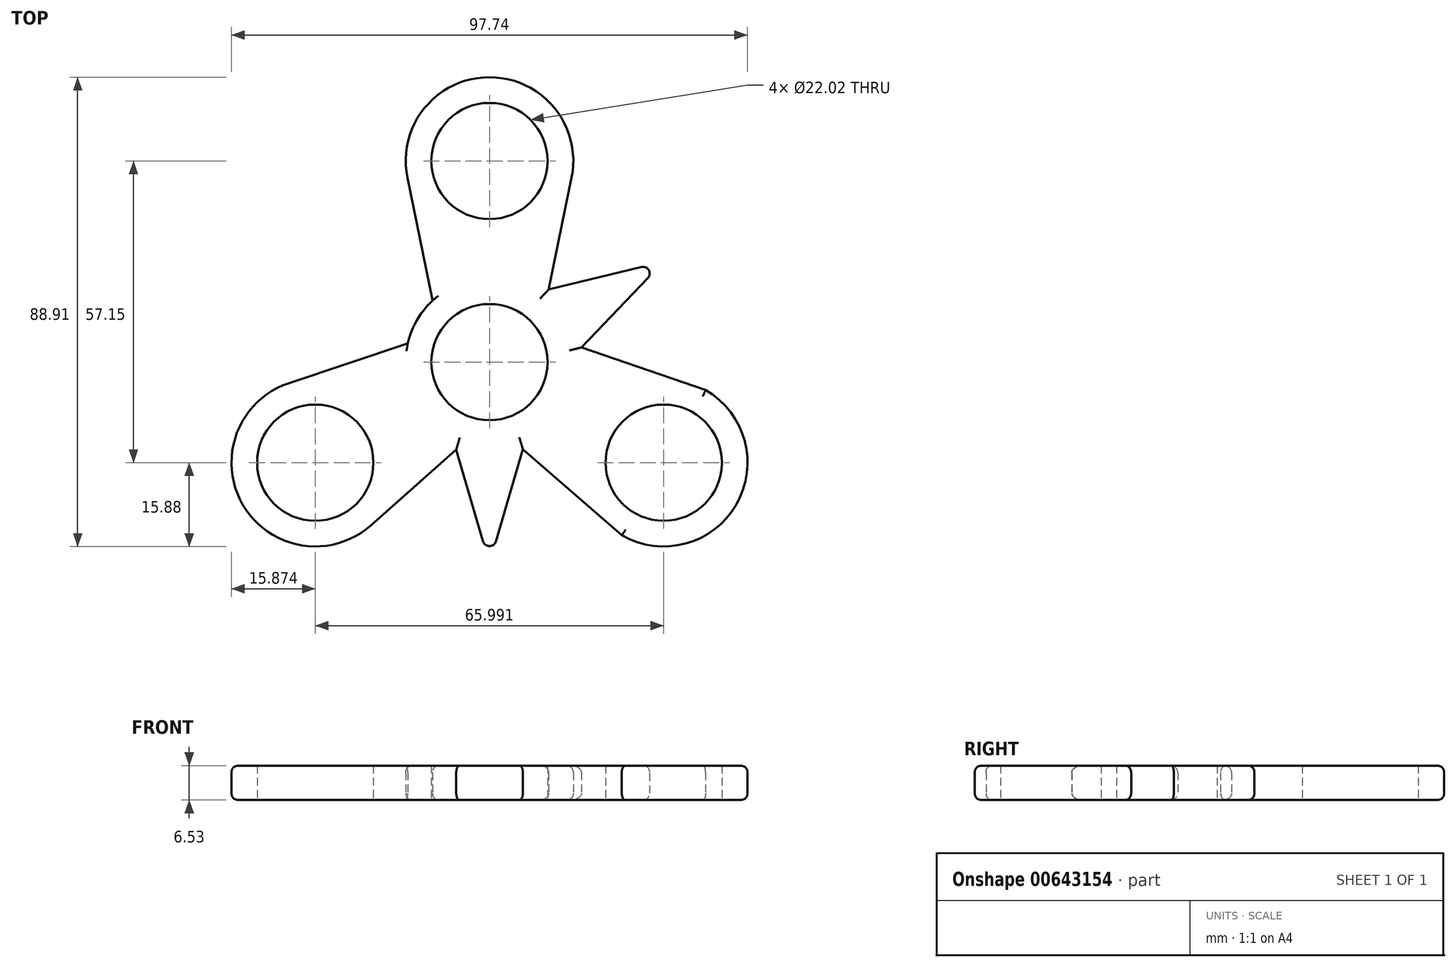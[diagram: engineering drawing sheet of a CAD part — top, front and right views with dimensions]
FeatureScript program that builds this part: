
annotation { "Feature Type Name" : "Feature", "Feature Type Description" : "" }
export const myFeature = defineFeature(function(context is Context, id is Id, definition is map)
    precondition{}
    {
        {
            var Q0;
            Q0=qCreatedBy(makeId("Top.planeOp"),FACE);
            var sketch = newSketch(context, id + "F0", { "sketchPlane" : qUnion([Q0])});
            skCircle(sketch, "E0", {"center": v(0, 0) * mm, "radius": 11.01 * mm});
            skLineSegment(sketch, "E1", {"start": v(0, 0) * mm, "end": v(0, 38.1) * mm});
            skLineSegment(sketch, "E2", {"start": v(0, 0) * mm, "end": v(33, -19.05) * mm});
            skLineSegment(sketch, "E3", {"start": v(0, 0) * mm, "end": v(-33, -19.05) * mm});
            skLineSegment(sketch, "E4", {"start": v(0, 0) * mm, "end": v(-33, 19.05) * mm});
            skLineSegment(sketch, "E5", {"start": v(-33, 19.05) * mm, "end": v(0, 0) * mm});
            skLineSegment(sketch, "E6", {"start": v(0, 0) * mm, "end": v(0, -38.1) * mm});
            skLineSegment(sketch, "E7", {"start": v(0, 0) * mm, "end": v(33, 19.05) * mm});
            skCircle(sketch, "E8", {"center": v(0, 38.1) * mm, "radius": 11.01 * mm});
            skCircle(sketch, "E9", {"center": v(33, -19.05) * mm, "radius": 11.01 * mm});
            skCircle(sketch, "E10", {"center": v(-33, -19.05) * mm, "radius": 11.01 * mm});
            skLineSegment(sketch, "E11", {"start": v(9.54, -5.5) * mm, "end": v(0, -38.1) * mm});
            skLineSegment(sketch, "E12", {"start": v(-9.54, -5.5) * mm, "end": v(0, -38.1) * mm});
            skLineSegment(sketch, "E13", {"start": v(-9.54, -5.5) * mm, "end": v(-33, 19.05) * mm});
            skLineSegment(sketch, "E14", {"start": v(0, 11.01) * mm, "end": v(-33, 19.05) * mm});
            skLineSegment(sketch, "E15", {"start": v(-9.54, 5.5) * mm, "end": v(-33, -19.05) * mm});
            skLineSegment(sketch, "E16", {"start": v(0, -11.01) * mm, "end": v(-33, -19.05) * mm});
            skLineSegment(sketch, "E17", {"start": v(9.54, 5.5) * mm, "end": v(33, -19.05) * mm});
            skLineSegment(sketch, "E18", {"start": v(0, -11.01) * mm, "end": v(33, -19.05) * mm});
            skLineSegment(sketch, "E19", {"start": v(0, 11.01) * mm, "end": v(33, 19.05) * mm});
            skLineSegment(sketch, "E20", {"start": v(9.54, -5.5) * mm, "end": v(33, 19.05) * mm});
            skLineSegment(sketch, "E21", {"start": v(9.54, 5.5) * mm, "end": v(0, 38.1) * mm});
            skLineSegment(sketch, "E22", {"start": v(-9.54, 5.5) * mm, "end": v(0, 38.1) * mm});
            skCircle(sketch, "E23", {"center": v(0, 0) * mm, "radius": 15.88 * mm});
            skCircle(sketch, "E24", {"center": v(0, 38.1) * mm, "radius": 15.88 * mm});
            skCircle(sketch, "E25", {"center": v(33, -19.05) * mm, "radius": 15.88 * mm});
            skCircle(sketch, "E26", {"center": v(-33, -19.05) * mm, "radius": 15.88 * mm});
            skLineSegment(sketch, "E27", {"start": v(-41.1, -5.02) * mm, "end": v(-24.9, -33.08) * mm});
            skLineSegment(sketch, "E28", {"start": v(-9.54, 5.5) * mm, "end": v(-41.1, -5.02) * mm});
            skLineSegment(sketch, "E29", {"start": v(0, -11.01) * mm, "end": v(-24.9, -33.08) * mm});
            skLineSegment(sketch, "E30", {"start": v(0, -11.01) * mm, "end": v(25.06, -32.8) * mm});
            skLineSegment(sketch, "E31", {"start": v(9.54, 5.5) * mm, "end": v(40.93, -5.3) * mm});
            skLineSegment(sketch, "E32", {"start": v(-16.2, 38.1) * mm, "end": v(16.2, 38.1) * mm});
            skLineSegment(sketch, "E33", {"start": v(9.54, 5.5) * mm, "end": v(16.2, 38.1) * mm});
            skLineSegment(sketch, "E34", {"start": v(-9.54, 5.5) * mm, "end": v(-16.2, 38.1) * mm});
            skLineSegment(sketch, "E35", {"start": v(25.06, -32.8) * mm, "end": v(40.93, -5.3) * mm});
            skSolve(sketch);
        }
        {
            var Q0;
            {var subQ0=sQuery(id+"F0.wireOp",EDGE,"E14");var subQ3=sQuery(id+"F0.wireOp",EDGE,"E22");var subQ5=makeQuery(id+"F0.imprint","INTERSECT",VERTEX,{"derivedFrom":[subQ0,subQ3]});Q0=makeQuery(id+"F0.imprint","IMPRINT",FACE,{"disambiguationData":[TD([[makeQuery(id+"F0.imprint","IMPRINT",EDGE,{"disambiguationData":[TD([[subQ5,1.0]])],"derivedFrom":subQ0}),1.0]])]});}
            var Q1;
            {var subQ1=sQuery(id+"F0.wireOp",EDGE,"E5");var subQ3=sQuery(id+"F0.wireOp",EDGE,"E23");var subQ4=makeQuery(id+"F0.imprint","INTERSECT",VERTEX,{"derivedFrom":[subQ1,subQ3]});Q1=makeQuery(id+"F0.imprint","IMPRINT",FACE,{"disambiguationData":[TD([[makeQuery(id+"F0.imprint","IMPRINT",EDGE,{"disambiguationData":[TD([[subQ4,1.0]])],"derivedFrom":subQ3}),-1.0]])]});}
            var Q2;
            {var subQ1=sQuery(id+"F0.wireOp",EDGE,"E5");var subQ3=sQuery(id+"F0.wireOp",EDGE,"E23");var subQ4=makeQuery(id+"F0.imprint","INTERSECT",VERTEX,{"derivedFrom":[subQ1,subQ3]});Q2=makeQuery(id+"F0.imprint","IMPRINT",FACE,{"disambiguationData":[TD([[makeQuery(id+"F0.imprint","IMPRINT",EDGE,{"disambiguationData":[TD([[subQ4,-1.0]])],"derivedFrom":subQ3}),-1.0]])]});}
            var Q3;
            {var subQ1=sQuery(id+"F0.wireOp",EDGE,"E5");var subQ3=sQuery(id+"F0.wireOp",EDGE,"E23");var subQ4=makeQuery(id+"F0.imprint","INTERSECT",VERTEX,{"derivedFrom":[subQ1,subQ3]});Q3=makeQuery(id+"F0.imprint","IMPRINT",FACE,{"disambiguationData":[TD([[makeQuery(id+"F0.imprint","IMPRINT",EDGE,{"disambiguationData":[TD([[subQ4,-1.0]])],"derivedFrom":subQ3}),1.0]])]});}
            var Q4;
            {var subQ0=sQuery(id+"F0.wireOp",EDGE,"E15");var subQ1=sQuery(id+"F0.wireOp",EDGE,"E13");var subQ2=makeQuery(id+"F0.imprint","INTERSECT",VERTEX,{"derivedFrom":[subQ1,subQ0]});Q4=makeQuery(id+"F0.imprint","IMPRINT",FACE,{"disambiguationData":[TD([[makeQuery(id+"F0.imprint","IMPRINT",EDGE,{"disambiguationData":[TD([[subQ2,-1.0]])],"derivedFrom":subQ1}),-1.0]])]});}
            var Q5;
            {var subQ0=sQuery(id+"F0.wireOp",EDGE,"E13");var subQ3=sQuery(id+"F0.wireOp",EDGE,"E15");var subQ5=makeQuery(id+"F0.imprint","INTERSECT",VERTEX,{"derivedFrom":[subQ0,subQ3]});Q5=makeQuery(id+"F0.imprint","IMPRINT",FACE,{"disambiguationData":[TD([[makeQuery(id+"F0.imprint","IMPRINT",EDGE,{"disambiguationData":[TD([[subQ5,1.0]])],"derivedFrom":subQ0}),-1.0]])]});}
            var Q6;
            {var subQ1=sQuery(id+"F0.wireOp",EDGE,"E5");var subQ3=sQuery(id+"F0.wireOp",EDGE,"E23");var subQ4=makeQuery(id+"F0.imprint","INTERSECT",VERTEX,{"derivedFrom":[subQ1,subQ3]});Q6=makeQuery(id+"F0.imprint","IMPRINT",FACE,{"disambiguationData":[TD([[makeQuery(id+"F0.imprint","IMPRINT",EDGE,{"disambiguationData":[TD([[subQ4,1.0]])],"derivedFrom":subQ3}),1.0]])]});}
            var Q7;
            {var subQ0=sQuery(id+"F0.wireOp",EDGE,"E34");var subQ1=sQuery(id+"F0.wireOp",EDGE,"E14");var subQ2=makeQuery(id+"F0.imprint","INTERSECT",VERTEX,{"derivedFrom":[subQ1,subQ0]});Q7=makeQuery(id+"F0.imprint","IMPRINT",FACE,{"disambiguationData":[TD([[makeQuery(id+"F0.imprint","IMPRINT",EDGE,{"disambiguationData":[TD([[subQ2,1.0]])],"derivedFrom":subQ1}),1.0]])]});}
            var Q8;
            {var subQ0=sQuery(id+"F0.wireOp",EDGE,"E22");var subQ1=sQuery(id+"F0.wireOp",EDGE,"E14");var subQ2=makeQuery(id+"F0.imprint","INTERSECT",VERTEX,{"derivedFrom":[subQ1,subQ0]});Q8=makeQuery(id+"F0.imprint","IMPRINT",FACE,{"disambiguationData":[TD([[makeQuery(id+"F0.imprint","IMPRINT",EDGE,{"disambiguationData":[TD([[subQ2,-1.0]])],"derivedFrom":subQ1}),1.0]])]});}
            var Q9;
            {var subQ0=sQuery(id+"F0.wireOp",EDGE,"E34");var subQ5=sQuery(id+"F0.wireOp",EDGE,"E14");var subQ6=makeQuery(id+"F0.imprint","INTERSECT",VERTEX,{"derivedFrom":[subQ5,subQ0]});Q9=makeQuery(id+"F0.imprint","IMPRINT",FACE,{"disambiguationData":[TD([[makeQuery(id+"F0.imprint","IMPRINT",EDGE,{"disambiguationData":[TD([[subQ6,1.0]])],"derivedFrom":subQ5}),-1.0]])]});}
            var Q10;
            {var subQ0=sQuery(id+"F0.wireOp",EDGE,"E23");var subQ1=sQuery(id+"F0.wireOp",EDGE,"E1");var subQ2=makeQuery(id+"F0.imprint","INTERSECT",VERTEX,{"derivedFrom":[subQ1,subQ0]});Q10=makeQuery(id+"F0.imprint","IMPRINT",FACE,{"disambiguationData":[TD([[makeQuery(id+"F0.imprint","IMPRINT",EDGE,{"disambiguationData":[TD([[subQ2,-1.0]])],"derivedFrom":subQ1}),1.0]])]});}
            var Q11;
            {var subQ0=sQuery(id+"F0.wireOp",EDGE,"E19");var subQ5=sQuery(id+"F0.wireOp",EDGE,"E21");var subQ6=makeQuery(id+"F0.imprint","INTERSECT",VERTEX,{"derivedFrom":[subQ0,subQ5]});Q11=makeQuery(id+"F0.imprint","IMPRINT",FACE,{"disambiguationData":[TD([[makeQuery(id+"F0.imprint","IMPRINT",EDGE,{"disambiguationData":[TD([[subQ6,-1.0]])],"derivedFrom":subQ5}),1.0]])]});}
            var Q12;
            {var subQ0=sQuery(id+"F0.wireOp",EDGE,"E14");var subQ5=sQuery(id+"F0.wireOp",EDGE,"E22");var subQ6=makeQuery(id+"F0.imprint","INTERSECT",VERTEX,{"derivedFrom":[subQ0,subQ5]});Q12=makeQuery(id+"F0.imprint","IMPRINT",FACE,{"disambiguationData":[TD([[makeQuery(id+"F0.imprint","IMPRINT",EDGE,{"disambiguationData":[TD([[subQ6,-1.0]])],"derivedFrom":subQ5}),-1.0]])]});}
            var Q13;
            {var subQ0=sQuery(id+"F0.wireOp",EDGE,"E22");var subQ1=sQuery(id+"F0.wireOp",EDGE,"E14");var subQ2=makeQuery(id+"F0.imprint","INTERSECT",VERTEX,{"derivedFrom":[subQ1,subQ0]});Q13=makeQuery(id+"F0.imprint","IMPRINT",FACE,{"disambiguationData":[TD([[makeQuery(id+"F0.imprint","IMPRINT",EDGE,{"disambiguationData":[TD([[subQ2,-1.0]])],"derivedFrom":subQ1}),-1.0]])]});}
            var Q14;
            {var subQ0=sQuery(id+"F0.wireOp",EDGE,"E28");var subQ1=sQuery(id+"F0.wireOp",EDGE,"E13");var subQ2=makeQuery(id+"F0.imprint","INTERSECT",VERTEX,{"derivedFrom":[subQ1,subQ0]});Q14=makeQuery(id+"F0.imprint","IMPRINT",FACE,{"disambiguationData":[TD([[makeQuery(id+"F0.imprint","IMPRINT",EDGE,{"disambiguationData":[TD([[subQ2,1.0]])],"derivedFrom":subQ1}),-1.0]])]});}
            var Q15;
            {var subQ0=sQuery(id+"F0.wireOp",EDGE,"E28");var subQ6=sQuery(id+"F0.wireOp",EDGE,"E13");var subQ9=makeQuery(id+"F0.imprint","INTERSECT",VERTEX,{"derivedFrom":[subQ6,subQ0]});Q15=makeQuery(id+"F0.imprint","IMPRINT",FACE,{"disambiguationData":[TD([[makeQuery(id+"F0.imprint","IMPRINT",EDGE,{"disambiguationData":[TD([[subQ9,1.0]])],"derivedFrom":subQ6}),1.0]])]});}
            var Q16;
            {var subQ0=sQuery(id+"F0.wireOp",EDGE,"E13");var subQ5=sQuery(id+"F0.wireOp",EDGE,"E15");var subQ6=makeQuery(id+"F0.imprint","INTERSECT",VERTEX,{"derivedFrom":[subQ0,subQ5]});Q16=makeQuery(id+"F0.imprint","IMPRINT",FACE,{"disambiguationData":[TD([[makeQuery(id+"F0.imprint","IMPRINT",EDGE,{"disambiguationData":[TD([[subQ6,-1.0]])],"derivedFrom":subQ5}),1.0]])]});}
            var Q17;
            {var subQ0=sQuery(id+"F0.wireOp",EDGE,"E15");var subQ1=sQuery(id+"F0.wireOp",EDGE,"E13");var subQ2=makeQuery(id+"F0.imprint","INTERSECT",VERTEX,{"derivedFrom":[subQ1,subQ0]});Q17=makeQuery(id+"F0.imprint","IMPRINT",FACE,{"disambiguationData":[TD([[makeQuery(id+"F0.imprint","IMPRINT",EDGE,{"disambiguationData":[TD([[subQ2,-1.0]])],"derivedFrom":subQ1}),1.0]])]});}
            var Q18;
            {var subQ0=sQuery(id+"F0.wireOp",EDGE,"E23");var subQ1=sQuery(id+"F0.wireOp",EDGE,"E3");var subQ2=makeQuery(id+"F0.imprint","INTERSECT",VERTEX,{"derivedFrom":[subQ1,subQ0]});Q18=makeQuery(id+"F0.imprint","IMPRINT",FACE,{"disambiguationData":[TD([[makeQuery(id+"F0.imprint","IMPRINT",EDGE,{"disambiguationData":[TD([[subQ2,-1.0]])],"derivedFrom":subQ1}),-1.0]])]});}
            var Q19;
            {var subQ0=sQuery(id+"F0.wireOp",EDGE,"E16");var subQ1=sQuery(id+"F0.wireOp",EDGE,"E12");var subQ2=makeQuery(id+"F0.imprint","INTERSECT",VERTEX,{"derivedFrom":[subQ1,subQ0]});Q19=makeQuery(id+"F0.imprint","IMPRINT",FACE,{"disambiguationData":[TD([[makeQuery(id+"F0.imprint","IMPRINT",EDGE,{"disambiguationData":[TD([[subQ2,-1.0]])],"derivedFrom":subQ1}),1.0]])]});}
            var Q20;
            {var subQ1=sQuery(id+"F0.wireOp",EDGE,"E6");var subQ3=sQuery(id+"F0.wireOp",EDGE,"E23");var subQ4=makeQuery(id+"F0.imprint","INTERSECT",VERTEX,{"derivedFrom":[subQ1,subQ3]});Q20=makeQuery(id+"F0.imprint","IMPRINT",FACE,{"disambiguationData":[TD([[makeQuery(id+"F0.imprint","IMPRINT",EDGE,{"disambiguationData":[TD([[subQ4,1.0]])],"derivedFrom":subQ3}),1.0]])]});}
            var Q21;
            {var subQ1=sQuery(id+"F0.wireOp",EDGE,"E6");var subQ3=sQuery(id+"F0.wireOp",EDGE,"E23");var subQ4=makeQuery(id+"F0.imprint","INTERSECT",VERTEX,{"derivedFrom":[subQ1,subQ3]});Q21=makeQuery(id+"F0.imprint","IMPRINT",FACE,{"disambiguationData":[TD([[makeQuery(id+"F0.imprint","IMPRINT",EDGE,{"disambiguationData":[TD([[subQ4,-1.0]])],"derivedFrom":subQ3}),1.0]])]});}
            var Q22;
            {var subQ0=sQuery(id+"F0.wireOp",EDGE,"E18");var subQ1=sQuery(id+"F0.wireOp",EDGE,"E11");var subQ2=makeQuery(id+"F0.imprint","INTERSECT",VERTEX,{"derivedFrom":[subQ1,subQ0]});Q22=makeQuery(id+"F0.imprint","IMPRINT",FACE,{"disambiguationData":[TD([[makeQuery(id+"F0.imprint","IMPRINT",EDGE,{"disambiguationData":[TD([[subQ2,-1.0]])],"derivedFrom":subQ1}),-1.0]])]});}
            var Q23;
            {var subQ0=sQuery(id+"F0.wireOp",EDGE,"E18");var subQ1=sQuery(id+"F0.wireOp",EDGE,"E11");var subQ2=makeQuery(id+"F0.imprint","INTERSECT",VERTEX,{"derivedFrom":[subQ1,subQ0]});Q23=makeQuery(id+"F0.imprint","IMPRINT",FACE,{"disambiguationData":[TD([[makeQuery(id+"F0.imprint","IMPRINT",EDGE,{"disambiguationData":[TD([[subQ2,-1.0]])],"derivedFrom":subQ1}),1.0]])]});}
            var Q24;
            {var subQ0=sQuery(id+"F0.wireOp",EDGE,"E16");var subQ1=sQuery(id+"F0.wireOp",EDGE,"E12");var subQ2=makeQuery(id+"F0.imprint","INTERSECT",VERTEX,{"derivedFrom":[subQ1,subQ0]});Q24=makeQuery(id+"F0.imprint","IMPRINT",FACE,{"disambiguationData":[TD([[makeQuery(id+"F0.imprint","IMPRINT",EDGE,{"disambiguationData":[TD([[subQ2,-1.0]])],"derivedFrom":subQ1}),-1.0]])]});}
            var Q25;
            {var subQ0=sQuery(id+"F0.wireOp",EDGE,"E12");var subQ3=sQuery(id+"F0.wireOp",EDGE,"E16");var subQ5=makeQuery(id+"F0.imprint","INTERSECT",VERTEX,{"derivedFrom":[subQ0,subQ3]});Q25=makeQuery(id+"F0.imprint","IMPRINT",FACE,{"disambiguationData":[TD([[makeQuery(id+"F0.imprint","IMPRINT",EDGE,{"disambiguationData":[TD([[subQ5,1.0]])],"derivedFrom":subQ0}),1.0]])]});}
            var Q26;
            {var subQ0=sQuery(id+"F0.wireOp",EDGE,"E12");var subQ5=sQuery(id+"F0.wireOp",EDGE,"E16");var subQ6=makeQuery(id+"F0.imprint","INTERSECT",VERTEX,{"derivedFrom":[subQ0,subQ5]});Q26=makeQuery(id+"F0.imprint","IMPRINT",FACE,{"disambiguationData":[TD([[makeQuery(id+"F0.imprint","IMPRINT",EDGE,{"disambiguationData":[TD([[subQ6,-1.0]])],"derivedFrom":subQ5}),-1.0]])]});}
            var Q27;
            {var subQ1=sQuery(id+"F0.wireOp",EDGE,"E7");var subQ3=sQuery(id+"F0.wireOp",EDGE,"E23");var subQ4=makeQuery(id+"F0.imprint","INTERSECT",VERTEX,{"derivedFrom":[subQ1,subQ3]});Q27=makeQuery(id+"F0.imprint","IMPRINT",FACE,{"disambiguationData":[TD([[makeQuery(id+"F0.imprint","IMPRINT",EDGE,{"disambiguationData":[TD([[subQ4,-1.0]])],"derivedFrom":subQ3}),1.0]])]});}
            var Q28;
            {var subQ1=sQuery(id+"F0.wireOp",EDGE,"E7");var subQ3=sQuery(id+"F0.wireOp",EDGE,"E23");var subQ4=makeQuery(id+"F0.imprint","INTERSECT",VERTEX,{"derivedFrom":[subQ1,subQ3]});Q28=makeQuery(id+"F0.imprint","IMPRINT",FACE,{"disambiguationData":[TD([[makeQuery(id+"F0.imprint","IMPRINT",EDGE,{"disambiguationData":[TD([[subQ4,1.0]])],"derivedFrom":subQ3}),1.0]])]});}
            var Q29;
            {var subQ1=sQuery(id+"F0.wireOp",EDGE,"E17");var subQ3=sQuery(id+"F0.wireOp",EDGE,"E20");var subQ4=makeQuery(id+"F0.imprint","INTERSECT",VERTEX,{"derivedFrom":[subQ1,subQ3]});Q29=makeQuery(id+"F0.imprint","IMPRINT",FACE,{"disambiguationData":[TD([[makeQuery(id+"F0.imprint","IMPRINT",EDGE,{"disambiguationData":[TD([[subQ4,-1.0]])],"derivedFrom":subQ3}),1.0]])]});}
            var Q30;
            {var subQ0=sQuery(id+"F0.wireOp",EDGE,"E20");var subQ3=sQuery(id+"F0.wireOp",EDGE,"E17");var subQ5=makeQuery(id+"F0.imprint","INTERSECT",VERTEX,{"derivedFrom":[subQ3,subQ0]});Q30=makeQuery(id+"F0.imprint","IMPRINT",FACE,{"disambiguationData":[TD([[makeQuery(id+"F0.imprint","IMPRINT",EDGE,{"disambiguationData":[TD([[subQ5,1.0]])],"derivedFrom":subQ0}),1.0]])]});}
            var Q31;
            {var subQ0=sQuery(id+"F0.wireOp",EDGE,"E20");var subQ5=sQuery(id+"F0.wireOp",EDGE,"E17");var subQ6=makeQuery(id+"F0.imprint","INTERSECT",VERTEX,{"derivedFrom":[subQ5,subQ0]});Q31=makeQuery(id+"F0.imprint","IMPRINT",FACE,{"disambiguationData":[TD([[makeQuery(id+"F0.imprint","IMPRINT",EDGE,{"disambiguationData":[TD([[subQ6,-1.0]])],"derivedFrom":subQ5}),-1.0]])]});}
            var Q32;
            {var subQ0=sQuery(id+"F0.wireOp",EDGE,"E11");var subQ5=sQuery(id+"F0.wireOp",EDGE,"E18");var subQ6=makeQuery(id+"F0.imprint","INTERSECT",VERTEX,{"derivedFrom":[subQ0,subQ5]});Q32=makeQuery(id+"F0.imprint","IMPRINT",FACE,{"disambiguationData":[TD([[makeQuery(id+"F0.imprint","IMPRINT",EDGE,{"disambiguationData":[TD([[subQ6,-1.0]])],"derivedFrom":subQ5}),1.0]])]});}
            var Q33;
            {var subQ0=sQuery(id+"F0.wireOp",EDGE,"E11");var subQ3=sQuery(id+"F0.wireOp",EDGE,"E18");var subQ5=makeQuery(id+"F0.imprint","INTERSECT",VERTEX,{"derivedFrom":[subQ0,subQ3]});Q33=makeQuery(id+"F0.imprint","IMPRINT",FACE,{"disambiguationData":[TD([[makeQuery(id+"F0.imprint","IMPRINT",EDGE,{"disambiguationData":[TD([[subQ5,1.0]])],"derivedFrom":subQ0}),-1.0]])]});}
            var Q34;
            {var subQ0=sQuery(id+"F0.wireOp",EDGE,"E20");var subQ1=sQuery(id+"F0.wireOp",EDGE,"E17");var subQ2=makeQuery(id+"F0.imprint","INTERSECT",VERTEX,{"derivedFrom":[subQ1,subQ0]});Q34=makeQuery(id+"F0.imprint","IMPRINT",FACE,{"disambiguationData":[TD([[makeQuery(id+"F0.imprint","IMPRINT",EDGE,{"disambiguationData":[TD([[subQ2,-1.0]])],"derivedFrom":subQ1}),1.0]])]});}
            var Q35;
            {var subQ0=sQuery(id+"F0.wireOp",EDGE,"E21");var subQ1=sQuery(id+"F0.wireOp",EDGE,"E19");var subQ2=makeQuery(id+"F0.imprint","INTERSECT",VERTEX,{"derivedFrom":[subQ1,subQ0]});Q35=makeQuery(id+"F0.imprint","IMPRINT",FACE,{"disambiguationData":[TD([[makeQuery(id+"F0.imprint","IMPRINT",EDGE,{"disambiguationData":[TD([[subQ2,-1.0]])],"derivedFrom":subQ1}),1.0]])]});}
            var Q36;
            {var subQ0=sQuery(id+"F0.wireOp",EDGE,"E21");var subQ1=sQuery(id+"F0.wireOp",EDGE,"E19");var subQ2=makeQuery(id+"F0.imprint","INTERSECT",VERTEX,{"derivedFrom":[subQ1,subQ0]});Q36=makeQuery(id+"F0.imprint","IMPRINT",FACE,{"disambiguationData":[TD([[makeQuery(id+"F0.imprint","IMPRINT",EDGE,{"disambiguationData":[TD([[subQ2,-1.0]])],"derivedFrom":subQ1}),-1.0]])]});}
            var Q37;
            {var subQ0=sQuery(id+"F0.wireOp",EDGE,"E19");var subQ3=sQuery(id+"F0.wireOp",EDGE,"E21");var subQ5=makeQuery(id+"F0.imprint","INTERSECT",VERTEX,{"derivedFrom":[subQ0,subQ3]});Q37=makeQuery(id+"F0.imprint","IMPRINT",FACE,{"disambiguationData":[TD([[makeQuery(id+"F0.imprint","IMPRINT",EDGE,{"disambiguationData":[TD([[subQ5,1.0]])],"derivedFrom":subQ0}),-1.0]])]});}
            var Q38;
            {var subQ1=sQuery(id+"F0.wireOp",EDGE,"E7");var subQ3=sQuery(id+"F0.wireOp",EDGE,"E23");var subQ4=makeQuery(id+"F0.imprint","INTERSECT",VERTEX,{"derivedFrom":[subQ1,subQ3]});Q38=makeQuery(id+"F0.imprint","IMPRINT",FACE,{"disambiguationData":[TD([[makeQuery(id+"F0.imprint","IMPRINT",EDGE,{"disambiguationData":[TD([[subQ4,-1.0]])],"derivedFrom":subQ3}),-1.0]])]});}
            var Q39;
            {var subQ1=sQuery(id+"F0.wireOp",EDGE,"E7");var subQ3=sQuery(id+"F0.wireOp",EDGE,"E23");var subQ4=makeQuery(id+"F0.imprint","INTERSECT",VERTEX,{"derivedFrom":[subQ1,subQ3]});Q39=makeQuery(id+"F0.imprint","IMPRINT",FACE,{"disambiguationData":[TD([[makeQuery(id+"F0.imprint","IMPRINT",EDGE,{"disambiguationData":[TD([[subQ4,1.0]])],"derivedFrom":subQ3}),-1.0]])]});}
            var Q40;
            {var subQ0=sQuery(id+"F0.wireOp",EDGE,"E33");var subQ1=sQuery(id+"F0.wireOp",EDGE,"E19");var subQ2=makeQuery(id+"F0.imprint","INTERSECT",VERTEX,{"derivedFrom":[subQ1,subQ0]});Q40=makeQuery(id+"F0.imprint","IMPRINT",FACE,{"disambiguationData":[TD([[makeQuery(id+"F0.imprint","IMPRINT",EDGE,{"disambiguationData":[TD([[subQ2,1.0]])],"derivedFrom":subQ1}),-1.0]])]});}
            var Q41;
            {var subQ0=sQuery(id+"F0.wireOp",EDGE,"E31");var subQ1=sQuery(id+"F0.wireOp",EDGE,"E20");var subQ2=makeQuery(id+"F0.imprint","INTERSECT",VERTEX,{"derivedFrom":[subQ1,subQ0]});Q41=makeQuery(id+"F0.imprint","IMPRINT",FACE,{"disambiguationData":[TD([[makeQuery(id+"F0.imprint","IMPRINT",EDGE,{"disambiguationData":[TD([[subQ2,1.0]])],"derivedFrom":subQ1}),1.0]])]});}
            var Q42;
            {var subQ0=sQuery(id+"F0.wireOp",EDGE,"E23");var subQ1=sQuery(id+"F0.wireOp",EDGE,"E2");var subQ2=makeQuery(id+"F0.imprint","INTERSECT",VERTEX,{"derivedFrom":[subQ1,subQ0]});Q42=makeQuery(id+"F0.imprint","IMPRINT",FACE,{"disambiguationData":[TD([[makeQuery(id+"F0.imprint","IMPRINT",EDGE,{"disambiguationData":[TD([[subQ2,-1.0]])],"derivedFrom":subQ1}),1.0]])]});}
            var Q43;
            {var subQ0=sQuery(id+"F0.wireOp",EDGE,"E23");var subQ1=sQuery(id+"F0.wireOp",EDGE,"E2");var subQ2=makeQuery(id+"F0.imprint","INTERSECT",VERTEX,{"derivedFrom":[subQ1,subQ0]});Q43=makeQuery(id+"F0.imprint","IMPRINT",FACE,{"disambiguationData":[TD([[makeQuery(id+"F0.imprint","IMPRINT",EDGE,{"disambiguationData":[TD([[subQ2,-1.0]])],"derivedFrom":subQ1}),-1.0]])]});}
            var Q44;
            {var subQ0=sQuery(id+"F0.wireOp",EDGE,"E30");var subQ6=sQuery(id+"F0.wireOp",EDGE,"E11");var subQ9=makeQuery(id+"F0.imprint","INTERSECT",VERTEX,{"derivedFrom":[subQ6,subQ0]});Q44=makeQuery(id+"F0.imprint","IMPRINT",FACE,{"disambiguationData":[TD([[makeQuery(id+"F0.imprint","IMPRINT",EDGE,{"disambiguationData":[TD([[subQ9,1.0]])],"derivedFrom":subQ6}),1.0]])]});}
            var Q45;
            {var subQ0=sQuery(id+"F0.wireOp",EDGE,"E25");var subQ1=sQuery(id+"F0.wireOp",EDGE,"E2");var subQ2=makeQuery(id+"F0.imprint","INTERSECT",VERTEX,{"derivedFrom":[subQ1,subQ0]});Q45=makeQuery(id+"F0.imprint","IMPRINT",FACE,{"disambiguationData":[TD([[makeQuery(id+"F0.imprint","IMPRINT",EDGE,{"disambiguationData":[TD([[subQ2,-1.0]])],"derivedFrom":subQ1}),1.0]])]});}
            var Q46;
            {var subQ0=sQuery(id+"F0.wireOp",EDGE,"E25");var subQ1=sQuery(id+"F0.wireOp",EDGE,"E2");var subQ2=makeQuery(id+"F0.imprint","INTERSECT",VERTEX,{"derivedFrom":[subQ1,subQ0]});Q46=makeQuery(id+"F0.imprint","IMPRINT",FACE,{"disambiguationData":[TD([[makeQuery(id+"F0.imprint","IMPRINT",EDGE,{"disambiguationData":[TD([[subQ2,-1.0]])],"derivedFrom":subQ1}),-1.0]])]});}
            var Q47;
            {var subQ4=sQuery(id+"F0.wireOp",EDGE,"E9");var subQ7=sQuery(id+"F0.wireOp",EDGE,"E18");var subQ9=makeQuery(id+"F0.imprint","INTERSECT",VERTEX,{"derivedFrom":[subQ4,subQ7]});Q47=makeQuery(id+"F0.imprint","IMPRINT",FACE,{"disambiguationData":[TD([[makeQuery(id+"F0.imprint","IMPRINT",EDGE,{"disambiguationData":[TD([[subQ9,-1.0]])],"derivedFrom":subQ4}),-1.0]])]});}
            var Q48;
            {var subQ5=sQuery(id+"F0.wireOp",EDGE,"E9");var subQ7=sQuery(id+"F0.wireOp",EDGE,"hszmHcWR-75RD-CN57-jphi-yZqC3nmjHUUF");var subQ8=makeQuery(id+"F0.imprint","INTERSECT",VERTEX,{"disambiguationData":[OD(0.0)],"derivedFrom":[subQ5,subQ7]});Q48=makeQuery(id+"F0.imprint","IMPRINT",FACE,{"disambiguationData":[TD([[makeQuery(id+"F0.imprint","IMPRINT",EDGE,{"disambiguationData":[TD([[subQ8,-1.0]])],"derivedFrom":subQ5}),-1.0]])]});}
            var Q49;
            {var subQ1=sQuery(id+"F0.wireOp",EDGE,"E6");var subQ3=sQuery(id+"F0.wireOp",EDGE,"E23");var subQ4=makeQuery(id+"F0.imprint","INTERSECT",VERTEX,{"derivedFrom":[subQ1,subQ3]});Q49=makeQuery(id+"F0.imprint","IMPRINT",FACE,{"disambiguationData":[TD([[makeQuery(id+"F0.imprint","IMPRINT",EDGE,{"disambiguationData":[TD([[subQ4,-1.0]])],"derivedFrom":subQ3}),-1.0]])]});}
            var Q50;
            {var subQ1=sQuery(id+"F0.wireOp",EDGE,"E6");var subQ3=sQuery(id+"F0.wireOp",EDGE,"E23");var subQ4=makeQuery(id+"F0.imprint","INTERSECT",VERTEX,{"derivedFrom":[subQ1,subQ3]});Q50=makeQuery(id+"F0.imprint","IMPRINT",FACE,{"disambiguationData":[TD([[makeQuery(id+"F0.imprint","IMPRINT",EDGE,{"disambiguationData":[TD([[subQ4,1.0]])],"derivedFrom":subQ3}),-1.0]])]});}
            var Q51;
            {var subQ0=sQuery(id+"F0.wireOp",EDGE,"E29");var subQ1=sQuery(id+"F0.wireOp",EDGE,"E12");var subQ2=makeQuery(id+"F0.imprint","INTERSECT",VERTEX,{"derivedFrom":[subQ1,subQ0]});Q51=makeQuery(id+"F0.imprint","IMPRINT",FACE,{"disambiguationData":[TD([[makeQuery(id+"F0.imprint","IMPRINT",EDGE,{"disambiguationData":[TD([[subQ2,1.0]])],"derivedFrom":subQ1}),1.0]])]});}
            var Q52;
            {var subQ0=sQuery(id+"F0.wireOp",EDGE,"E30");var subQ1=sQuery(id+"F0.wireOp",EDGE,"E11");var subQ2=makeQuery(id+"F0.imprint","INTERSECT",VERTEX,{"derivedFrom":[subQ1,subQ0]});Q52=makeQuery(id+"F0.imprint","IMPRINT",FACE,{"disambiguationData":[TD([[makeQuery(id+"F0.imprint","IMPRINT",EDGE,{"disambiguationData":[TD([[subQ2,1.0]])],"derivedFrom":subQ1}),-1.0]])]});}
            var Q53;
            {var subQ3=sQuery(id+"F0.wireOp",EDGE,"E17");var subQ7=sQuery(id+"F0.wireOp",EDGE,"E23");var subQ9=makeQuery(id+"F0.imprint","INTERSECT",VERTEX,{"derivedFrom":[subQ3,subQ7]});Q53=makeQuery(id+"F0.imprint","IMPRINT",FACE,{"disambiguationData":[TD([[makeQuery(id+"F0.imprint","IMPRINT",EDGE,{"disambiguationData":[TD([[subQ9,-1.0]])],"derivedFrom":subQ3}),1.0]])]});}
            var Q54;
            {var subQ0=sQuery(id+"F0.wireOp",EDGE,"E23");var subQ1=sQuery(id+"F0.wireOp",EDGE,"E3");var subQ2=makeQuery(id+"F0.imprint","INTERSECT",VERTEX,{"derivedFrom":[subQ1,subQ0]});Q54=makeQuery(id+"F0.imprint","IMPRINT",FACE,{"disambiguationData":[TD([[makeQuery(id+"F0.imprint","IMPRINT",EDGE,{"disambiguationData":[TD([[subQ2,-1.0]])],"derivedFrom":subQ1}),1.0]])]});}
            var Q55;
            {var subQ1=sQuery(id+"F0.wireOp",EDGE,"E12");var subQ5=sQuery(id+"F0.wireOp",EDGE,"E29");var subQ9=makeQuery(id+"F0.imprint","INTERSECT",VERTEX,{"derivedFrom":[subQ1,subQ5]});Q55=makeQuery(id+"F0.imprint","IMPRINT",FACE,{"disambiguationData":[TD([[makeQuery(id+"F0.imprint","IMPRINT",EDGE,{"disambiguationData":[TD([[subQ9,1.0]])],"derivedFrom":subQ1}),-1.0]])]});}
            var Q56;
            {var subQ0=sQuery(id+"F0.wireOp",EDGE,"E26");var subQ1=sQuery(id+"F0.wireOp",EDGE,"E3");var subQ2=makeQuery(id+"F0.imprint","INTERSECT",VERTEX,{"derivedFrom":[subQ1,subQ0]});Q56=makeQuery(id+"F0.imprint","IMPRINT",FACE,{"disambiguationData":[TD([[makeQuery(id+"F0.imprint","IMPRINT",EDGE,{"disambiguationData":[TD([[subQ2,-1.0]])],"derivedFrom":subQ1}),1.0]])]});}
            var Q57;
            {var subQ0=sQuery(id+"F0.wireOp",EDGE,"E26");var subQ1=sQuery(id+"F0.wireOp",EDGE,"E3");var subQ2=makeQuery(id+"F0.imprint","INTERSECT",VERTEX,{"derivedFrom":[subQ1,subQ0]});Q57=makeQuery(id+"F0.imprint","IMPRINT",FACE,{"disambiguationData":[TD([[makeQuery(id+"F0.imprint","IMPRINT",EDGE,{"disambiguationData":[TD([[subQ2,-1.0]])],"derivedFrom":subQ1}),-1.0]])]});}
            var Q58;
            {var subQ4=sQuery(id+"F0.wireOp",EDGE,"E15");var subQ6=sQuery(id+"F0.wireOp",EDGE,"E10");var subQ7=makeQuery(id+"F0.imprint","INTERSECT",VERTEX,{"derivedFrom":[subQ6,subQ4]});Q58=makeQuery(id+"F0.imprint","IMPRINT",FACE,{"disambiguationData":[TD([[makeQuery(id+"F0.imprint","IMPRINT",EDGE,{"disambiguationData":[TD([[subQ7,-1.0]])],"derivedFrom":subQ6}),-1.0]])]});}
            var Q59;
            {var subQ2=sQuery(id+"F0.wireOp",EDGE,"E16");var subQ4=sQuery(id+"F0.wireOp",EDGE,"E10");var subQ5=makeQuery(id+"F0.imprint","INTERSECT",VERTEX,{"derivedFrom":[subQ4,subQ2]});Q59=makeQuery(id+"F0.imprint","IMPRINT",FACE,{"disambiguationData":[TD([[makeQuery(id+"F0.imprint","IMPRINT",EDGE,{"disambiguationData":[TD([[subQ5,1.0]])],"derivedFrom":subQ4}),-1.0]])]});}
            var Q60;
            {var subQ0=sQuery(id+"F0.wireOp",EDGE,"E27");var subQ1=sQuery(id+"F0.wireOp",EDGE,"E10");var subQ2=makeQuery(id+"F0.imprint","INTERSECT",VERTEX,{"disambiguationData":[OD(0.0)],"derivedFrom":[subQ1,subQ0]});Q60=makeQuery(id+"F0.imprint","IMPRINT",FACE,{"disambiguationData":[TD([[makeQuery(id+"F0.imprint","IMPRINT",EDGE,{"disambiguationData":[TD([[subQ2,-1.0]])],"derivedFrom":subQ1}),-1.0]])]});}
            var Q61;
            {var subQ5=sQuery(id+"F0.wireOp",EDGE,"E33");var subQ7=sQuery(id+"F0.wireOp",EDGE,"E19");var subQ9=makeQuery(id+"F0.imprint","INTERSECT",VERTEX,{"derivedFrom":[subQ7,subQ5]});Q61=makeQuery(id+"F0.imprint","IMPRINT",FACE,{"disambiguationData":[TD([[makeQuery(id+"F0.imprint","IMPRINT",EDGE,{"disambiguationData":[TD([[subQ9,1.0]])],"derivedFrom":subQ7}),1.0]])]});}
            var Q62;
            {var subQ0=sQuery(id+"F0.wireOp",EDGE,"E23");var subQ1=sQuery(id+"F0.wireOp",EDGE,"E1");var subQ2=makeQuery(id+"F0.imprint","INTERSECT",VERTEX,{"derivedFrom":[subQ1,subQ0]});Q62=makeQuery(id+"F0.imprint","IMPRINT",FACE,{"disambiguationData":[TD([[makeQuery(id+"F0.imprint","IMPRINT",EDGE,{"disambiguationData":[TD([[subQ2,-1.0]])],"derivedFrom":subQ1}),-1.0]])]});}
            var Q63;
            {var subQ0=sQuery(id+"F0.wireOp",EDGE,"E32");var subQ1=sQuery(id+"F0.wireOp",EDGE,"E8");var subQ2=makeQuery(id+"F0.imprint","INTERSECT",VERTEX,{"disambiguationData":[OD(0.0)],"derivedFrom":[subQ1,subQ0]});Q63=makeQuery(id+"F0.imprint","IMPRINT",FACE,{"disambiguationData":[TD([[makeQuery(id+"F0.imprint","IMPRINT",EDGE,{"disambiguationData":[TD([[subQ2,1.0]])],"derivedFrom":subQ1}),-1.0]])]});}
            var Q64;
            {var subQ4=sQuery(id+"F0.wireOp",EDGE,"E8");var subQ6=sQuery(id+"F0.wireOp",EDGE,"E32");var subQ8=makeQuery(id+"F0.imprint","INTERSECT",VERTEX,{"disambiguationData":[OD(1.0)],"derivedFrom":[subQ4,subQ6]});Q64=makeQuery(id+"F0.imprint","IMPRINT",FACE,{"disambiguationData":[TD([[makeQuery(id+"F0.imprint","IMPRINT",EDGE,{"disambiguationData":[TD([[subQ8,1.0]])],"derivedFrom":subQ4}),-1.0]])]});}
            var Q65;
            {var subQ4=sQuery(id+"F0.wireOp",EDGE,"E32");var subQ6=sQuery(id+"F0.wireOp",EDGE,"E8");var subQ8=makeQuery(id+"F0.imprint","INTERSECT",VERTEX,{"disambiguationData":[OD(0.0)],"derivedFrom":[subQ6,subQ4]});Q65=makeQuery(id+"F0.imprint","IMPRINT",FACE,{"disambiguationData":[TD([[makeQuery(id+"F0.imprint","IMPRINT",EDGE,{"disambiguationData":[TD([[subQ8,-1.0]])],"derivedFrom":subQ6}),-1.0]])]});}
            var Q66;
            {var subQ0=sQuery(id+"F0.wireOp",EDGE,"E24");var subQ1=sQuery(id+"F0.wireOp",EDGE,"E1");var subQ2=makeQuery(id+"F0.imprint","INTERSECT",VERTEX,{"derivedFrom":[subQ1,subQ0]});Q66=makeQuery(id+"F0.imprint","IMPRINT",FACE,{"disambiguationData":[TD([[makeQuery(id+"F0.imprint","IMPRINT",EDGE,{"disambiguationData":[TD([[subQ2,-1.0]])],"derivedFrom":subQ1}),1.0]])]});}
            var Q67;
            {var subQ0=sQuery(id+"F0.wireOp",EDGE,"E24");var subQ1=sQuery(id+"F0.wireOp",EDGE,"E1");var subQ2=makeQuery(id+"F0.imprint","INTERSECT",VERTEX,{"derivedFrom":[subQ1,subQ0]});Q67=makeQuery(id+"F0.imprint","IMPRINT",FACE,{"disambiguationData":[TD([[makeQuery(id+"F0.imprint","IMPRINT",EDGE,{"disambiguationData":[TD([[subQ2,-1.0]])],"derivedFrom":subQ1}),-1.0]])]});}
            var Q68;
            {var subQ3=sQuery(id+"F0.wireOp",EDGE,"E17");var subQ5=sQuery(id+"F0.wireOp",EDGE,"E9");var subQ6=makeQuery(id+"F0.imprint","INTERSECT",VERTEX,{"derivedFrom":[subQ5,subQ3]});Q68=makeQuery(id+"F0.imprint","IMPRINT",FACE,{"disambiguationData":[TD([[makeQuery(id+"F0.imprint","IMPRINT",EDGE,{"disambiguationData":[TD([[subQ6,1.0]])],"derivedFrom":subQ5}),-1.0]])]});}
            var Q69;
            {var subQ0=sQuery(id+"F0.wireOp",EDGE,"E35");var subQ1=sQuery(id+"F0.wireOp",EDGE,"E9");var subQ2=makeQuery(id+"F0.imprint","INTERSECT",VERTEX,{"disambiguationData":[OD(0.0)],"derivedFrom":[subQ1,subQ0]});Q69=makeQuery(id+"F0.imprint","IMPRINT",FACE,{"disambiguationData":[TD([[makeQuery(id+"F0.imprint","IMPRINT",EDGE,{"disambiguationData":[TD([[subQ2,1.0]])],"derivedFrom":subQ1}),-1.0]])]});}
            extrude(context, id + "F1", {"entities" : qUnion([Q0, Q1, Q2, Q3, Q4, Q5, Q6, Q7, Q8, Q9, Q10, Q11, Q12, Q13, Q14, Q15, Q16, Q17, Q18, Q19, Q20, Q21, Q22, Q23, Q24, Q25, Q26, Q27, Q28, Q29, Q30, Q31, Q32, Q33, Q34, Q35, Q36, Q37, Q38, Q39, Q40, Q41, Q42, Q43, Q44, Q45, Q46, Q47, Q48, Q49, Q50, Q51, Q52, Q53, Q54, Q55, Q56, Q57, Q58, Q59, Q60, Q61, Q62, Q63, Q64, Q65, Q66, Q67, Q68, Q69]), "depth" : 6.53 * mm, "offsetDistance" : 25.4 * mm});
        }
        {
            var Q0;
            Q0=makeQuery(id+"F1.opExtrude","CAP_EDGE",EDGE,{"disambiguationData":[OSD([sQuery(id+"F0.wireOp",EDGE,"E24")])],"isStart":false});
            var Q1;
            Q1=makeQuery(id+"F1.opExtrude","CAP_EDGE",EDGE,{"disambiguationData":[OSD([sQuery(id+"F0.wireOp",EDGE,"E34")])],"isStart":false});
            var Q2;
            Q2=makeQuery(id+"F1.opExtrude","CAP_EDGE",EDGE,{"disambiguationData":[OSD([sQuery(id+"F0.wireOp",EDGE,"E14")])],"isStart":false});
            var Q3;
            Q3=makeQuery(id+"F1.opExtrude","CAP_EDGE",EDGE,{"disambiguationData":[OSD([sQuery(id+"F0.wireOp",EDGE,"E13")])],"isStart":false});
            var Q4;
            Q4=makeQuery(id+"F1.opExtrude","CAP_EDGE",EDGE,{"disambiguationData":[OSD([sQuery(id+"F0.wireOp",EDGE,"E28")])],"isStart":false});
            var Q5;
            Q5=makeQuery(id+"F1.opExtrude","CAP_EDGE",EDGE,{"disambiguationData":[OSD([sQuery(id+"F0.wireOp",EDGE,"E26")])],"isStart":false});
            var Q6;
            Q6=makeQuery(id+"F1.opExtrude","CAP_EDGE",EDGE,{"disambiguationData":[OSD([sQuery(id+"F0.wireOp",EDGE,"E29")])],"isStart":false});
            var Q7;
            Q7=makeQuery(id+"F1.opExtrude","CAP_EDGE",EDGE,{"disambiguationData":[OSD([sQuery(id+"F0.wireOp",EDGE,"E12")])],"isStart":false});
            var Q8;
            Q8=makeQuery(id+"F1.opExtrude","CAP_EDGE",EDGE,{"disambiguationData":[OSD([sQuery(id+"F0.wireOp",EDGE,"E11")])],"isStart":false});
            var Q9;
            Q9=makeQuery(id+"F1.opExtrude","CAP_EDGE",EDGE,{"disambiguationData":[OSD([sQuery(id+"F0.wireOp",EDGE,"E30")])],"isStart":false});
            var Q10;
            Q10=makeQuery(id+"F1.opExtrude","CAP_EDGE",EDGE,{"disambiguationData":[OSD([sQuery(id+"F0.wireOp",EDGE,"E25")])],"isStart":false});
            var Q11;
            Q11=makeQuery(id+"F1.opExtrude","CAP_EDGE",EDGE,{"disambiguationData":[OSD([sQuery(id+"F0.wireOp",EDGE,"E31")])],"isStart":false});
            var Q12;
            Q12=makeQuery(id+"F1.opExtrude","CAP_EDGE",EDGE,{"disambiguationData":[OSD([sQuery(id+"F0.wireOp",EDGE,"E20")])],"isStart":false});
            var Q13;
            Q13=makeQuery(id+"F1.opExtrude","CAP_EDGE",EDGE,{"disambiguationData":[OSD([sQuery(id+"F0.wireOp",EDGE,"E19")])],"isStart":false});
            var Q14;
            Q14=makeQuery(id+"F1.opExtrude","CAP_EDGE",EDGE,{"disambiguationData":[OSD([sQuery(id+"F0.wireOp",EDGE,"E33")])],"isStart":false});
            var Q15;
            Q15=makeQuery(id+"F1.opExtrude","CAP_EDGE",EDGE,{"disambiguationData":[OSD([sQuery(id+"F0.wireOp",EDGE,"E34")])],"isStart":true});
            var Q16;
            Q16=makeQuery(id+"F1.opExtrude","CAP_EDGE",EDGE,{"disambiguationData":[OSD([sQuery(id+"F0.wireOp",EDGE,"E24")])],"isStart":true});
            var Q17;
            Q17=makeQuery(id+"F1.opExtrude","CAP_EDGE",EDGE,{"disambiguationData":[OSD([sQuery(id+"F0.wireOp",EDGE,"E33")])],"isStart":true});
            var Q18;
            Q18=makeQuery(id+"F1.opExtrude","CAP_EDGE",EDGE,{"disambiguationData":[OSD([sQuery(id+"F0.wireOp",EDGE,"E19")])],"isStart":true});
            var Q19;
            Q19=makeQuery(id+"F1.opExtrude","CAP_EDGE",EDGE,{"disambiguationData":[OSD([sQuery(id+"F0.wireOp",EDGE,"E20")])],"isStart":true});
            var Q20;
            Q20=makeQuery(id+"F1.opExtrude","CAP_EDGE",EDGE,{"disambiguationData":[OSD([sQuery(id+"F0.wireOp",EDGE,"E31")])],"isStart":true});
            var Q21;
            Q21=makeQuery(id+"F1.opExtrude","CAP_EDGE",EDGE,{"disambiguationData":[OSD([sQuery(id+"F0.wireOp",EDGE,"E30")])],"isStart":true});
            var Q22;
            Q22=makeQuery(id+"F1.opExtrude","CAP_EDGE",EDGE,{"disambiguationData":[OSD([sQuery(id+"F0.wireOp",EDGE,"E25")])],"isStart":true});
            var Q23;
            Q23=makeQuery(id+"F1.opExtrude","CAP_EDGE",EDGE,{"disambiguationData":[OSD([sQuery(id+"F0.wireOp",EDGE,"E11")])],"isStart":true});
            var Q24;
            Q24=makeQuery(id+"F1.opExtrude","CAP_EDGE",EDGE,{"disambiguationData":[OSD([sQuery(id+"F0.wireOp",EDGE,"E12")])],"isStart":true});
            var Q25;
            Q25=makeQuery(id+"F1.opExtrude","CAP_EDGE",EDGE,{"disambiguationData":[OSD([sQuery(id+"F0.wireOp",EDGE,"E29")])],"isStart":true});
            var Q26;
            Q26=makeQuery(id+"F1.opExtrude","CAP_EDGE",EDGE,{"disambiguationData":[OSD([sQuery(id+"F0.wireOp",EDGE,"E26")])],"isStart":true});
            var Q27;
            Q27=makeQuery(id+"F1.opExtrude","CAP_EDGE",EDGE,{"disambiguationData":[OSD([sQuery(id+"F0.wireOp",EDGE,"E13")])],"isStart":true});
            var Q28;
            Q28=makeQuery(id+"F1.opExtrude","CAP_EDGE",EDGE,{"disambiguationData":[OSD([sQuery(id+"F0.wireOp",EDGE,"E14")])],"isStart":true});
            fillet(context, id + "F2", {"entities" : qUnion([Q0, Q1, Q2, Q3, Q4, Q5, Q6, Q7, Q8, Q9, Q10, Q11, Q12, Q13, Q14, Q15, Q16, Q17, Q18, Q19, Q20, Q21, Q22, Q23, Q24, Q25, Q26, Q27, Q28]), "radius" : 1.27 * mm, "tangentPropagation" : true, "allowEdgeOverflow" : false});
        }
        {
            var Q0;
            Q0=makeQuery(id+"F1.opExtrude","SWEPT_EDGE",EDGE,{"disambiguationData":[OSD([sQuery(id+"F0.wireOp",EDGE,"E7"),sQuery(id+"F0.wireOp",EDGE,"E19"),sQuery(id+"F0.wireOp",EDGE,"E20")])]});
            var Q1;
            Q1=makeQuery(id+"F1.opExtrude","SWEPT_EDGE",EDGE,{"disambiguationData":[OSD([sQuery(id+"F0.wireOp",EDGE,"E5"),sQuery(id+"F0.wireOp",EDGE,"E13"),sQuery(id+"F0.wireOp",EDGE,"E14")])]});
            var Q2;
            Q2=makeQuery(id+"F1.opExtrude","SWEPT_EDGE",EDGE,{"disambiguationData":[OSD([sQuery(id+"F0.wireOp",EDGE,"E6"),sQuery(id+"F0.wireOp",EDGE,"E11"),sQuery(id+"F0.wireOp",EDGE,"E12")])]});
            fillet(context, id + "F3", {"entities" : qUnion([Q0, Q1, Q2]), "radius" : 1.27 * mm, "tangentPropagation" : true, "allowEdgeOverflow" : false});
        }
    });
